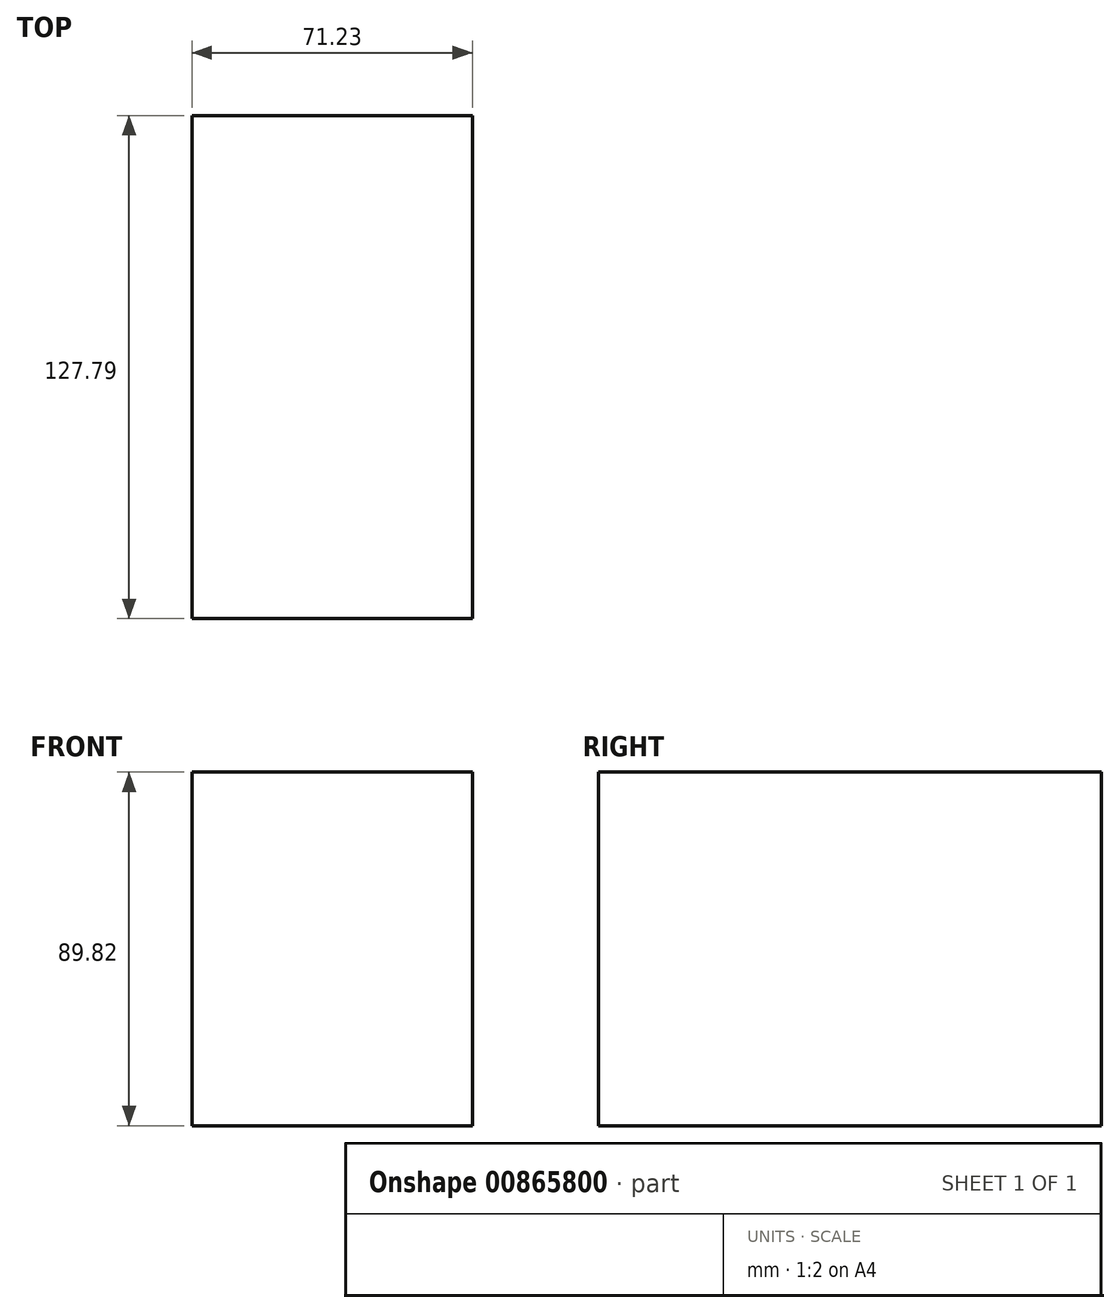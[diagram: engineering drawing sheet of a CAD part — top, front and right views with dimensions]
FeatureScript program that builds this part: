
annotation { "Feature Type Name" : "Feature", "Feature Type Description" : "" }
export const myFeature = defineFeature(function(context is Context, id is Id, definition is map)
    precondition{}
    {
        {
            var Q0;
            Q0=qCreatedBy(makeId("Top.planeOp"),FACE);
            var sketch = newSketch(context, id + "F0", { "sketchPlane" : qUnion([Q0])});
            skLineSegment(sketch, "E0.bottom", {"start": v(-25.46, 101.3) * mm, "end": v(45.77, 101.3) * mm});
            skLineSegment(sketch, "E0.top", {"start": v(-25.46, -26.49) * mm, "end": v(45.77, -26.49) * mm});
            skLineSegment(sketch, "E0.left", {"start": v(-25.46, 101.3) * mm, "end": v(-25.46, -26.49) * mm});
            skLineSegment(sketch, "E0.right", {"start": v(45.77, 101.3) * mm, "end": v(45.77, -26.49) * mm});
            skSolve(sketch);
        }
        {
            var Q0;
            Q0=makeQuery(id+"F0.imprint","IMPRINT",FACE,{"disambiguationData":[TD([[makeQuery(id+"F0.imprint","IMPRINT",EDGE,{"derivedFrom":sQuery(id+"F0.wireOp",EDGE,"E0.bottom")}),-1.0]])]});
            extrude(context, id + "F1", {"entities" : qUnion([Q0]), "depth" : 89.82 * mm, "offsetDistance" : 25.4 * mm});
        }
    });
